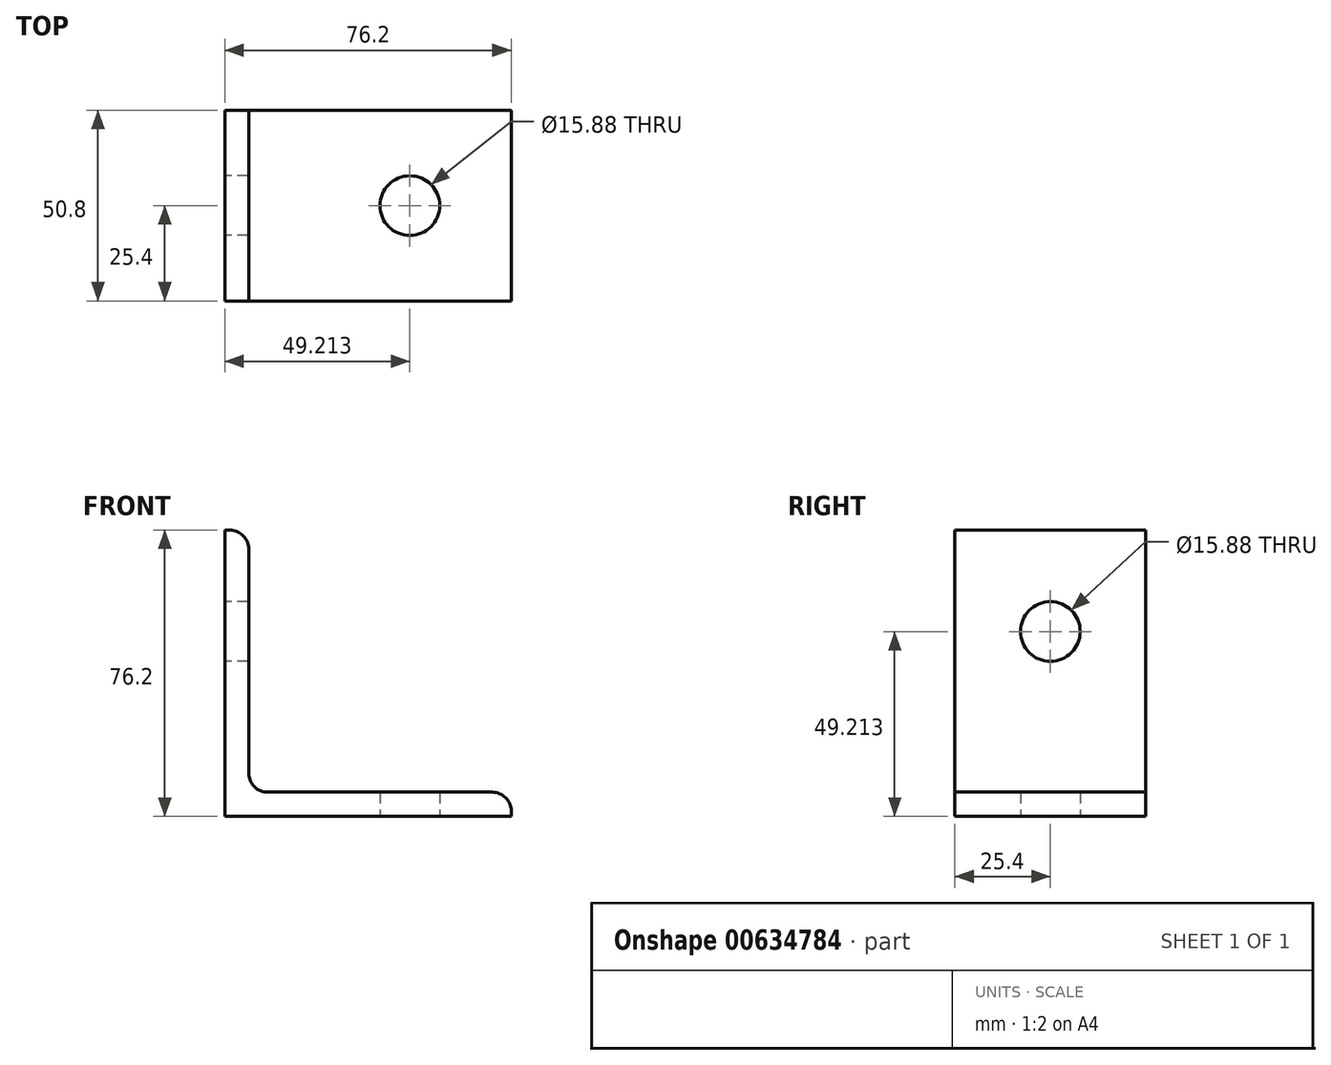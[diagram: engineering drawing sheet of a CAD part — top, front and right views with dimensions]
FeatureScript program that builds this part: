
annotation { "Feature Type Name" : "Feature", "Feature Type Description" : "" }
export const myFeature = defineFeature(function(context is Context, id is Id, definition is map)
    precondition{}
    {
        {
            var Q0;
            Q0=qCreatedBy(makeId("Front.planeOp"),FACE);
            var sketch = newSketch(context, id + "F0", { "sketchPlane" : qUnion([Q0])});
            skLineSegment(sketch, "E0.bottom", {"start": v(38.1, -38.1) * mm, "end": v(-38.1, -38.1) * mm});
            skLineSegment(sketch, "E0.top", {"start": v(-31.75, 38.1) * mm, "end": v(-38.1, 38.1) * mm});
            skLineSegment(sketch, "E0.left", {"start": v(38.1, -38.1) * mm, "end": v(38.1, -31.67) * mm});
            skLineSegment(sketch, "E0.right", {"start": v(-38.1, -38.1) * mm, "end": v(-38.1, 38.1) * mm});
            skPoint(sketch, "E0.middle", {"position": v(0, 0) * mm});
            skLineSegment(sketch, "E1.0", {"start": v(-31.75, -31.67) * mm, "end": v(-31.75, 38.1) * mm});
            skLineSegment(sketch, "E2.0", {"start": v(38.1, -31.67) * mm, "end": v(-31.75, -31.67) * mm});
            skPoint(sketch, "E3.orphan", {"position": v(38.1, 38.1) * mm});
            skSolve(sketch);
        }
        {
            var Q0;
            Q0 = qSketchRegion(id + "F0", true);
            extrude(context, id + "F1", {"entities" : qUnion([Q0]), "endBound" : BoundingType.SYMMETRIC, "depth" : 50.8 * mm, "offsetDistance" : 25.4 * mm});
        }
        {
            var Q0;
            Q0=makeQuery(id+"F1.opExtrude","SWEPT_EDGE",EDGE,{"disambiguationData":[OSD([sQuery(id+"F0.wireOp",EDGE,"E0.top"),sQuery(id+"F0.wireOp",EDGE,"E1.0")])]});
            var Q1;
            Q1=makeQuery(id+"F1.opExtrude","SWEPT_EDGE",EDGE,{"disambiguationData":[OSD([sQuery(id+"F0.wireOp",EDGE,"E1.0"),sQuery(id+"F0.wireOp",EDGE,"E2.0")])]});
            var Q2;
            Q2=makeQuery(id+"F1.opExtrude","SWEPT_EDGE",EDGE,{"disambiguationData":[OSD([sQuery(id+"F0.wireOp",EDGE,"E0.left"),sQuery(id+"F0.wireOp",EDGE,"E2.0")])]});
            fillet(context, id + "F2", {"entities" : qUnion([Q0, Q1, Q2]), "radius" : 5.08 * mm, "tangentPropagation" : true, "allowEdgeOverflow" : false});
        }
        {
            var Q0;
            Q0=makeQuery(id+"F1.opExtrude","SWEPT_FACE",FACE,{"disambiguationData":[OSD([sQuery(id+"F0.wireOp",EDGE,"E0.right")])]});
            var sketch = newSketch(context, id + "F3", { "sketchPlane" : qUnion([Q0])});
            skCircle(sketch, "E4", {"center": v(0, 11.11) * mm, "radius": 7.94 * mm});
            skSolve(sketch);
        }
        {
            var Q0;
            Q0 = qSketchRegion(id + "F3", true);
            extrude(context, id + "F4", {"entities" : qUnion([Q0]), "operationType" : NewBodyOperationType.REMOVE, "oppositeDirection" : true, "depth" : 25.4 * mm, "offsetDistance" : 25.4 * mm});
        }
        {
            var Q0;
            Q0=makeQuery(id+"F1.opExtrude","SWEPT_FACE",FACE,{"disambiguationData":[OSD([sQuery(id+"F0.wireOp",EDGE,"E0.bottom")])]});
            var sketch = newSketch(context, id + "F5", { "sketchPlane" : qUnion([Q0])});
            skCircle(sketch, "E5", {"center": v(11.11, 0) * mm, "radius": 7.94 * mm});
            skSolve(sketch);
        }
        {
            var Q0;
            Q0 = qSketchRegion(id + "F5", true);
            extrude(context, id + "F6", {"entities" : qUnion([Q0]), "operationType" : NewBodyOperationType.REMOVE, "oppositeDirection" : true, "depth" : 25.4 * mm, "offsetDistance" : 25.4 * mm});
        }
    });
